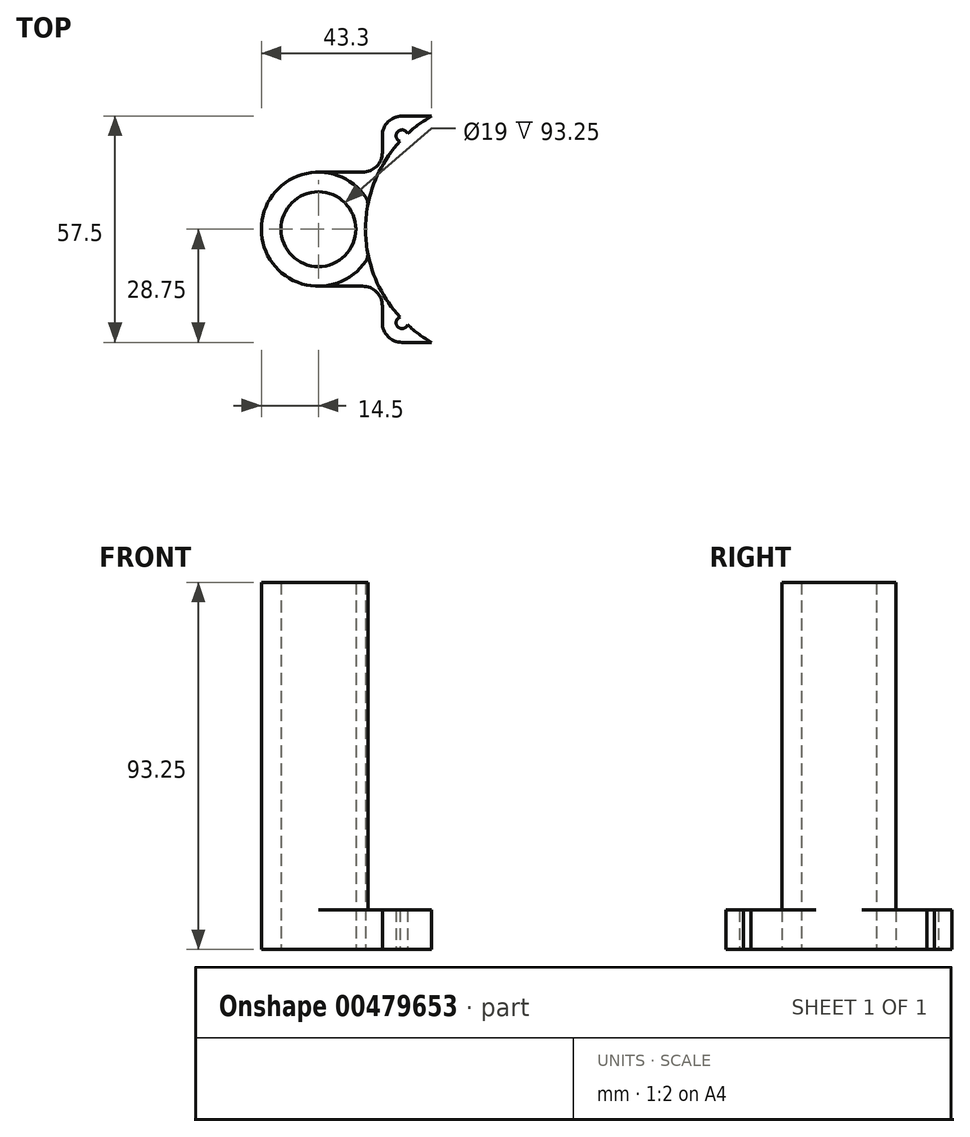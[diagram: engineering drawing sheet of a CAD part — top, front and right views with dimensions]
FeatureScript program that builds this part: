
annotation { "Feature Type Name" : "Feature", "Feature Type Description" : "" }
export const myFeature = defineFeature(function(context is Context, id is Id, definition is map)
    precondition{}
    {
        {
            var Q0;
            Q0=qCreatedBy(makeId("Top.planeOp"),FACE);
            var sketch = newSketch(context, id + "F0", { "sketchPlane" : qUnion([Q0])});
            skPoint(sketch, "E0.middle", {"position": v(0, 0) * mm});
            skCircle(sketch, "E1", {"center": v(-45, 0) * mm, "radius": 9.5 * mm});
            skArc(sketch, "E2.0", {"start": v(-45, 14.5) * mm, "mid": v(-59.5, 0) * mm, "end": v(-45, -14.5) * mm});
            skArc(sketch, "E3.MirrorC", {"start": v(45, 14.5) * mm, "mid": v(59.5, 0) * mm, "end": v(45, -14.5) * mm});
            skCircle(sketch, "E4.MirrorC", {"center": v(45, 0) * mm, "radius": 9.5 * mm});
            skPoint(sketch, "E5.trimOffspring.end.orphan", {"position": v(-45, 9.75) * mm});
            skPoint(sketch, "E6.trimOffspring.end.orphan", {"position": v(-45, -9.75) * mm});
            skPoint(sketch, "E0.top.start.orphan", {"position": v(45, -9.75) * mm});
            skPoint(sketch, "E0.bottom.start.orphan", {"position": v(45, 9.75) * mm});
            skLineSegment(sketch, "E7.bottom", {"start": v(23.75, 28.75) * mm, "end": v(16.2, 28.75) * mm});
            skLineSegment(sketch, "E7.top", {"start": v(23.75, -28.75) * mm, "end": v(16.2, -28.75) * mm});
            skLineSegment(sketch, "E7.left", {"start": v(28.75, 23.75) * mm, "end": v(28.75, 19.5) * mm});
            skLineSegment(sketch, "E7.right", {"start": v(-28.75, 23.75) * mm, "end": v(-28.75, 19.5) * mm});
            skLineSegment(sketch, "E8", {"start": v(-45, 0) * mm, "end": v(45, 0) * mm});
            skPoint(sketch, "E9.visualSharp", {"position": v(28.75, 28.75) * mm});
            skArc(sketch, "E9.filletArc", {"start": v(28.75, 23.75) * mm, "mid": v(27.29, 27.29) * mm, "end": v(23.75, 28.75) * mm});
            skPoint(sketch, "E10.visualSharp", {"position": v(-28.75, 28.75) * mm});
            skArc(sketch, "E10.filletArc", {"start": v(-23.75, 28.75) * mm, "mid": v(-27.29, 27.29) * mm, "end": v(-28.75, 23.75) * mm});
            skPoint(sketch, "E11.visualSharp", {"position": v(-28.75, -28.75) * mm});
            skArc(sketch, "E11.filletArc", {"start": v(-28.75, -23.75) * mm, "mid": v(-27.29, -27.29) * mm, "end": v(-23.75, -28.75) * mm});
            skPoint(sketch, "E12.visualSharp", {"position": v(28.75, -28.75) * mm});
            skArc(sketch, "E12.filletArc", {"start": v(23.75, -28.75) * mm, "mid": v(27.29, -27.29) * mm, "end": v(28.75, -23.75) * mm});
            skPoint(sketch, "E13.center.orphan", {"position": v(-28.75, 0) * mm});
            skPoint(sketch, "E14.visualSharp", {"position": v(-28.75, 23.75) * mm});
            skCircle(sketch, "E15", {"center": v(-23.75, 23.75) * mm, "radius": 1.5 * mm});
            skCircle(sketch, "E16.MirrorC", {"center": v(23.75, 23.75) * mm, "radius": 1.5 * mm});
            skLineSegment(sketch, "E17.MirrorCS", {"start": v(45, 0) * mm, "end": v(-45, 0) * mm});
            skCircle(sketch, "E18.MirrorC", {"center": v(-23.75, -23.75) * mm, "radius": 1.5 * mm});
            skCircle(sketch, "E19.MirrorC", {"center": v(23.75, -23.75) * mm, "radius": 1.5 * mm});
            skLineSegment(sketch, "E20", {"start": v(45, 14.5) * mm, "end": v(33.75, 14.5) * mm});
            skPoint(sketch, "E21.MirrorCS.end.orphan", {"position": v(31, 22.69) * mm});
            skPoint(sketch, "E21.MirrorCS.start.orphan", {"position": v(51.21, 13.1) * mm});
            skPoint(sketch, "E22.MirrorCS.end.orphan", {"position": v(28.44, 25.48) * mm});
            skArc(sketch, "E23.filletArc", {"start": v(28.75, 19.5) * mm, "mid": v(30.21, 15.96) * mm, "end": v(33.75, 14.5) * mm});
            skPoint(sketch, "E24.MirrorCS.end.orphan", {"position": v(31, -22.69) * mm});
            skPoint(sketch, "E24.MirrorCS.start.orphan", {"position": v(51.21, -13.1) * mm});
            skPoint(sketch, "E25.MirrorCS.end.orphan", {"position": v(28.44, -25.48) * mm});
            skPoint(sketch, "E26.start.orphan", {"position": v(-51.21, 13.1) * mm});
            skPoint(sketch, "E14.filletArc.end.orphan", {"position": v(-28.44, 25.48) * mm});
            skPoint(sketch, "E14.filletArc.start.orphan", {"position": v(-31, 22.69) * mm});
            skPoint(sketch, "E27.MirrorCS.end.orphan", {"position": v(-31, -22.69) * mm});
            skPoint(sketch, "E27.MirrorCS.start.orphan", {"position": v(-51.21, -13.1) * mm});
            skPoint(sketch, "E28.MirrorCS.end.orphan", {"position": v(-28.44, -25.48) * mm});
            skArc(sketch, "E29.MirrorCS", {"start": v(-28.75, 19.5) * mm, "mid": v(-30.21, 15.96) * mm, "end": v(-33.75, 14.5) * mm});
            skLineSegment(sketch, "E30.MirrorCS", {"start": v(-45, 14.5) * mm, "end": v(-33.75, 14.5) * mm});
            skLineSegment(sketch, "E31.MirrorCS", {"start": v(-45, -14.5) * mm, "end": v(-33.75, -14.5) * mm});
            skArc(sketch, "E32.MirrorCS", {"start": v(-28.75, -19.5) * mm, "mid": v(-30.21, -15.96) * mm, "end": v(-33.75, -14.5) * mm});
            skArc(sketch, "E33.MirrorCS", {"start": v(28.75, -19.5) * mm, "mid": v(30.21, -15.96) * mm, "end": v(33.75, -14.5) * mm});
            skLineSegment(sketch, "E34.MirrorCS", {"start": v(45, -14.5) * mm, "end": v(33.75, -14.5) * mm});
            skLineSegment(sketch, "E35", {"start": v(28.75, -23.75) * mm, "end": v(28.75, -19.5) * mm});
            skLineSegment(sketch, "E36.trimOffspring", {"start": v(-28.75, -19.5) * mm, "end": v(-28.75, -23.75) * mm});
            skCircle(sketch, "E37", {"center": v(0, 0) * mm, "radius": 30 * mm});
            skArc(sketch, "E38.0", {"start": v(-22.35, -24.28) * mm, "mid": v(0, -33) * mm, "end": v(22.35, -24.28) * mm});
            skLineSegment(sketch, "E39.trimOffspring", {"start": v(-16.2, 28.75) * mm, "end": v(-23.75, 28.75) * mm});
            skLineSegment(sketch, "E40.trimOffspring", {"start": v(-16.2, -28.75) * mm, "end": v(-23.75, -28.75) * mm});
            skArc(sketch, "E41.trimOffspring", {"start": v(24.28, -22.35) * mm, "mid": v(33, 0) * mm, "end": v(24.28, 22.35) * mm});
            skArc(sketch, "E42.trimOffspring", {"start": v(22.35, 24.28) * mm, "mid": v(0, 33) * mm, "end": v(-22.35, 24.28) * mm});
            skArc(sketch, "E43.trimOffspring", {"start": v(-24.28, 22.35) * mm, "mid": v(-33, 0) * mm, "end": v(-24.28, -22.35) * mm});
            skSolve(sketch);
        }
        {
            var Q0;
            Q0=makeQuery(id+"F0.imprint","IMPRINT",FACE,{"disambiguationData":[TD([[makeQuery(id+"F0.imprint","IMPRINT",EDGE,{"derivedFrom":sQuery(id+"F0.wireOp",EDGE,"E1")}),-1.0]])]});
            var Q1;
            Q1=makeQuery(id+"F0.imprint","IMPRINT",FACE,{"disambiguationData":[TD([[makeQuery(id+"F0.imprint","IMPRINT",EDGE,{"derivedFrom":sQuery(id+"F0.wireOp",EDGE,"E3.MirrorC")}),-1.0]])]});
            var Q2;
            {var subQ5=sQuery(id+"F0.wireOp",EDGE,"E41.trimOffspring");var subQ9=sQuery(id+"F0.wireOp",EDGE,"E17.MirrorCS");var subQ13=makeQuery(id+"F0.imprint","INTERSECT",VERTEX,{"derivedFrom":[subQ9,subQ5]});Q2=makeQuery(id+"F0.imprint","IMPRINT",FACE,{"disambiguationData":[TD([[makeQuery(id+"F0.imprint","IMPRINT",EDGE,{"disambiguationData":[TD([[subQ13,-1.0]])],"derivedFrom":subQ9}),-1.0]])]});}
            var Q3;
            {var subQ5=sQuery(id+"F0.wireOp",EDGE,"E17.MirrorCS");var subQ13=sQuery(id+"F0.wireOp",EDGE,"E41.trimOffspring");var subQ15=makeQuery(id+"F0.imprint","INTERSECT",VERTEX,{"derivedFrom":[subQ5,subQ13]});Q3=makeQuery(id+"F0.imprint","IMPRINT",FACE,{"disambiguationData":[TD([[makeQuery(id+"F0.imprint","IMPRINT",EDGE,{"disambiguationData":[TD([[subQ15,-1.0]])],"derivedFrom":subQ5}),1.0]])]});}
            var Q4;
            Q4 = qSketchRegion(id + "F2", true);
            extrude(context, id + "F1", {"entities" : qUnion([Q0, Q1, Q2, Q3, Q4]), "depth" : 10 * mm, "offsetDistance" : 25 * mm});
        }
        {
            var Q0;
            Q0=makeQuery(id+"F1.opExtrude","CAP_FACE",FACE,{"disambiguationData":[OSD([sQuery(id+"F0.wireOp",EDGE,"E1"),sQuery(id+"F0.wireOp",EDGE,"E2.0"),sQuery(id+"F0.wireOp",EDGE,"E3.MirrorC"),sQuery(id+"F0.wireOp",EDGE,"E4.MirrorC"),sQuery(id+"F0.wireOp",EDGE,"E7.bottom"),sQuery(id+"F0.wireOp",EDGE,"E7.top"),sQuery(id+"F0.wireOp",EDGE,"E7.left"),sQuery(id+"F0.wireOp",EDGE,"E7.right"),sQuery(id+"F0.wireOp",EDGE,"E9.filletArc"),sQuery(id+"F0.wireOp",EDGE,"E10.filletArc"),sQuery(id+"F0.wireOp",EDGE,"E11.filletArc"),sQuery(id+"F0.wireOp",EDGE,"E12.filletArc"),sQuery(id+"F0.wireOp",EDGE,"E16.MirrorC"),sQuery(id+"F0.wireOp",EDGE,"E15"),sQuery(id+"F0.wireOp",EDGE,"E18.MirrorC"),sQuery(id+"F0.wireOp",EDGE,"E19.MirrorC"),sQuery(id+"F0.wireOp",EDGE,"E20"),sQuery(id+"F0.wireOp",EDGE,"E23.filletArc"),sQuery(id+"F0.wireOp",EDGE,"E29.MirrorCS"),sQuery(id+"F0.wireOp",EDGE,"E30.MirrorCS"),sQuery(id+"F0.wireOp",EDGE,"E31.MirrorCS"),sQuery(id+"F0.wireOp",EDGE,"E32.MirrorCS"),sQuery(id+"F0.wireOp",EDGE,"E33.MirrorCS"),sQuery(id+"F0.wireOp",EDGE,"E34.MirrorCS"),sQuery(id+"F0.wireOp",EDGE,"E35"),sQuery(id+"F0.wireOp",EDGE,"E36.trimOffspring"),sQuery(id+"F0.wireOp",EDGE,"E37"),sQuery(id+"F0.wireOp",EDGE,"E38.0"),sQuery(id+"F0.wireOp",EDGE,"E39.trimOffspring"),sQuery(id+"F0.wireOp",EDGE,"E40.trimOffspring"),sQuery(id+"F0.wireOp",EDGE,"E42.trimOffspring")])],"isStart":false});
            var sketch = newSketch(context, id + "F2", { "sketchPlane" : qUnion([Q0])});
            skCircle(sketch, "E44.0", {"center": v(0, 0) * mm, "radius": 33 * mm});
            skCircle(sketch, "E45.0", {"center": v(-45, 0) * mm, "radius": 14.5 * mm});
            skCircle(sketch, "E46.0", {"center": v(45, 0) * mm, "radius": 14.5 * mm});
            skSolve(sketch);
        }
        {
            var Q0;
            Q0=makeQuery(id+"F2.imprint","IMPRINT",FACE,{"disambiguationData":[TD([[makeQuery(id+"F2.imprint","IMPRINT",EDGE,{"derivedFrom":makeQuery(id+"F1.opExtrude","CAP_EDGE",EDGE,{"disambiguationData":[OSD([sQuery(id+"F0.wireOp",EDGE,"E1")])],"isStart":false})}),-1.0]])]});
            var Q1;
            Q1=makeQuery(id+"F2.imprint","IMPRINT",FACE,{"disambiguationData":[TD([[makeQuery(id+"F2.imprint","IMPRINT",EDGE,{"derivedFrom":makeQuery(id+"F1.opExtrude","CAP_EDGE",EDGE,{"disambiguationData":[OSD([sQuery(id+"F0.wireOp",EDGE,"E4.MirrorC")])],"isStart":false})}),1.0]])]});
            extrude(context, id + "F3", {"entities" : qUnion([Q0, Q1]), "operationType" : NewBodyOperationType.ADD, "depth" : 83.25 * mm, "offsetDistance" : 25 * mm});
        }
        {
            var Q0;
            {var subQ0=sQuery(id+"F2.wireOp",EDGE,"E45.0");var subQ1=sQuery(id+"F2.wireOp",EDGE,"E44.0");Q0=makeQuery(id+"F3.opExtrude","SWEPT_EDGE",EDGE,{"disambiguationData":[OSD([subQ1,subQ0]),TDD([makeQuery(id+"F2.imprint","INTERSECT",VERTEX,{"disambiguationData":[OD(1.0)],"derivedFrom":[subQ1,subQ0]})])]});}
            var Q1;
            {var subQ0=sQuery(id+"F2.wireOp",EDGE,"E46.0");var subQ1=sQuery(id+"F2.wireOp",EDGE,"E44.0");Q1=makeQuery(id+"F3.opExtrude","SWEPT_EDGE",EDGE,{"disambiguationData":[OSD([subQ1,subQ0]),TDD([makeQuery(id+"F2.imprint","INTERSECT",VERTEX,{"disambiguationData":[OD(1.0)],"derivedFrom":[subQ1,subQ0]})])]});}
            var Q2;
            {var subQ0=sQuery(id+"F2.wireOp",EDGE,"E45.0");var subQ1=sQuery(id+"F2.wireOp",EDGE,"E44.0");Q2=makeQuery(id+"F3.opExtrude","SWEPT_EDGE",EDGE,{"disambiguationData":[OSD([subQ1,subQ0]),TDD([makeQuery(id+"F2.imprint","INTERSECT",VERTEX,{"disambiguationData":[OD(0.0)],"derivedFrom":[subQ1,subQ0]})])]});}
            var Q3;
            {var subQ0=sQuery(id+"F2.wireOp",EDGE,"E46.0");var subQ1=sQuery(id+"F2.wireOp",EDGE,"E44.0");Q3=makeQuery(id+"F3.opExtrude","SWEPT_EDGE",EDGE,{"disambiguationData":[OSD([subQ1,subQ0]),TDD([makeQuery(id+"F2.imprint","INTERSECT",VERTEX,{"disambiguationData":[OD(0.0)],"derivedFrom":[subQ1,subQ0]})])]});}
            fillet(context, id + "F4", {"entities" : qUnion([Q0, Q1, Q2, Q3]), "radius" : 3 * mm, "tangentPropagation" : true, "allowEdgeOverflow" : false});
        }
    });
